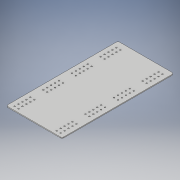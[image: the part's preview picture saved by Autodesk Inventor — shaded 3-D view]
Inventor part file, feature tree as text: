
AUTODESK INVENTOR PART (.ipt)
format: ipt  version: 2019.4 (Build 234330000, 330)  size: 199,680 bytes
history: native  units: in
note: dims shown in document units (in); Inventor stores cm internally (conversion verified against a paired STEP export)
features: sketch x2, extrude x1, hole x1, fillet x1
ambient origin geometry x8: Origin, YZ Plane, XZ Plane, XY Plane, X Axis, Y Axis, Z Axis, Center Point
bodies: Solid1 (feature_tree)
feature tree (5):
  extrude  "Extrusion1"  Depth=8.0in
  hole  "Hole1"  [1 undecoded]
  fillet  "Fillet1"  Radius=0.25in
  sketch  "Sketch1"  dims[d0=4.0in d1=8.0in]
  sketch  "Sketch2"  dims[d2=0.0625in d3=0.0in d4=0.35in d5=0.25in d6=1.9685in d8=0.2812in d9=0.7874in d11=0.2812in d14=0.0938in d15=0.273in d16=0.375in d17=0.25in d18=0.5635in d19=1.0in d20=0.8108in d21=1.5748in d23=2.055in d24=0.7874in d26=3.0185in d29=0.125in d30=0.3503in]
note: 1 required parameter value undecoded (feature->parameter linkage not recoverable at this tier; creation-order binding heuristic only, values carry confidence <= 0.55)
